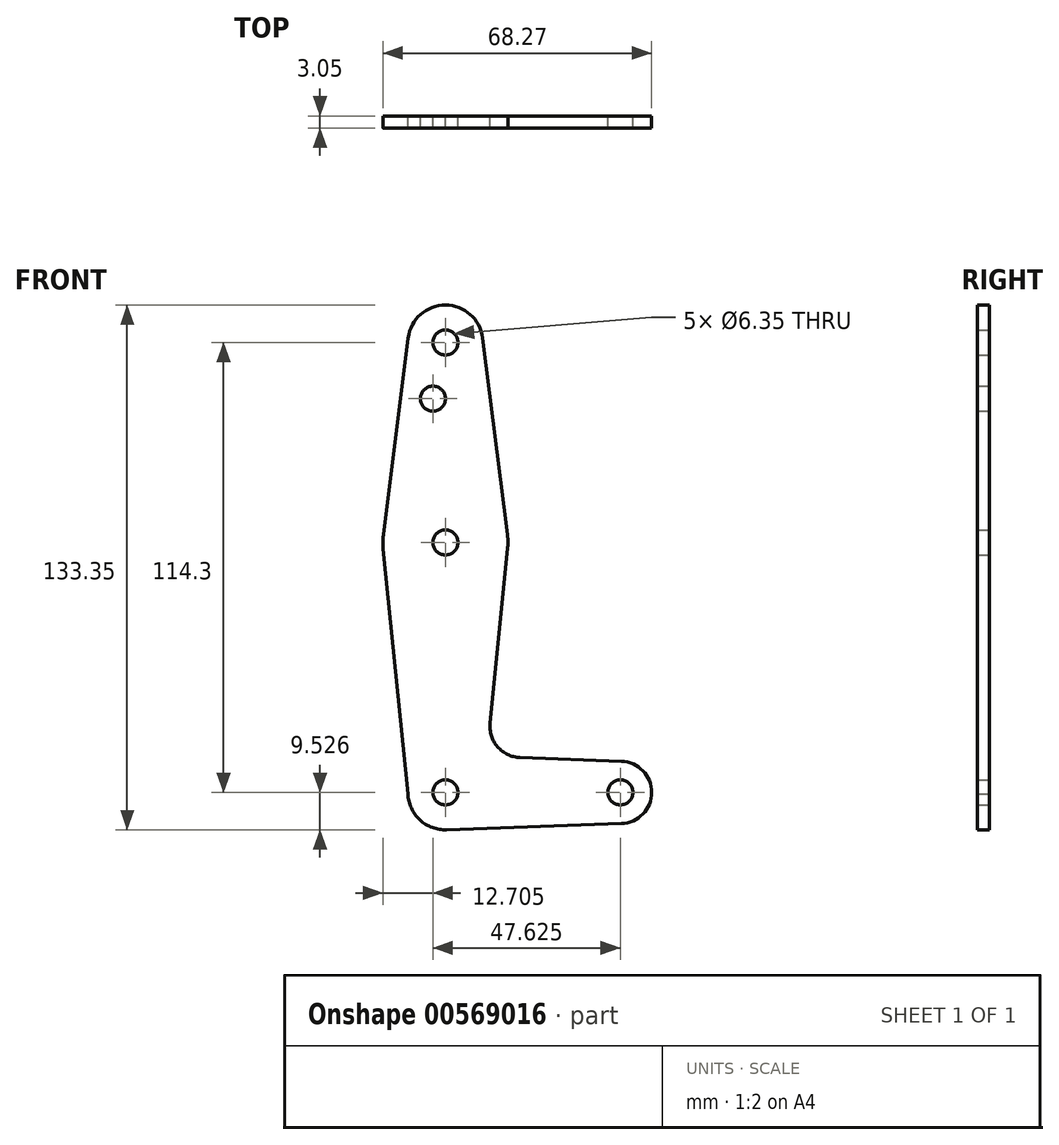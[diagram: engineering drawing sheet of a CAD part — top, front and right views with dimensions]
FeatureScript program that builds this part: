
annotation { "Feature Type Name" : "Feature", "Feature Type Description" : "" }
export const myFeature = defineFeature(function(context is Context, id is Id, definition is map)
    precondition{}
    {
        {
            var Q0;
            Q0=qCreatedBy(makeId("Front.planeOp"),FACE);
            var sketch = newSketch(context, id + "F0", { "sketchPlane" : qUnion([Q0])});
            skLineSegment(sketch, "E0", {"start": v(-33.37, 62.73) * mm, "end": v(-33.37, -51.57) * mm, "construction": true});
            skLineSegment(sketch, "E1", {"start": v(-33.37, -51.57) * mm, "end": v(11.08, -51.57) * mm, "construction": true});
            skCircle(sketch, "E2", {"center": v(-33.37, 62.73) * mm, "radius": 9.53 * mm});
            skCircle(sketch, "E3", {"center": v(-33.37, 11.93) * mm, "radius": 15.88 * mm});
            skCircle(sketch, "E4", {"center": v(-33.37, -51.57) * mm, "radius": 9.53 * mm});
            skCircle(sketch, "E5", {"center": v(11.08, -51.57) * mm, "radius": 7.94 * mm});
            skLineSegment(sketch, "E6", {"start": v(-42.82, 63.92) * mm, "end": v(-49.12, 13.91) * mm});
            skLineSegment(sketch, "E7", {"start": v(-49.16, 10.33) * mm, "end": v(-42.76, -53.16) * mm});
            skLineSegment(sketch, "E8", {"start": v(-14.4, -42.72) * mm, "end": v(11.36, -43.64) * mm});
            skLineSegment(sketch, "E9", {"start": v(-17.57, 10.34) * mm, "end": v(-22.03, -33.98) * mm});
            skLineSegment(sketch, "E10", {"start": v(-17.57, 13.55) * mm, "end": v(-23.92, 63.92) * mm});
            skCircle(sketch, "E11", {"center": v(-33.37, 62.73) * mm, "radius": 3.18 * mm});
            skCircle(sketch, "E12", {"center": v(-36.55, 48.45) * mm, "radius": 3.18 * mm});
            skCircle(sketch, "E13", {"center": v(-33.37, 11.93) * mm, "radius": 3.18 * mm});
            skCircle(sketch, "E14", {"center": v(-33.37, -51.57) * mm, "radius": 3.18 * mm});
            skCircle(sketch, "E15", {"center": v(11.08, -51.57) * mm, "radius": 3.18 * mm});
            skArc(sketch, "E16.filletArc", {"start": v(-22.03, -33.98) * mm, "mid": v(-20.1, -40) * mm, "end": v(-14.4, -42.72) * mm});
            skLineSegment(sketch, "E17", {"start": v(-33.44, -61.1) * mm, "end": v(11.36, -59.5) * mm});
            skSolve(sketch);
        }
        {
            var Q0;
            Q0 = qSketchRegion(id + "F0", true);
            extrude(context, id + "F1", {"entities" : qUnion([Q0]), "depth" : 3.05 * mm, "offsetDistance" : 25.4 * mm});
        }
    });
